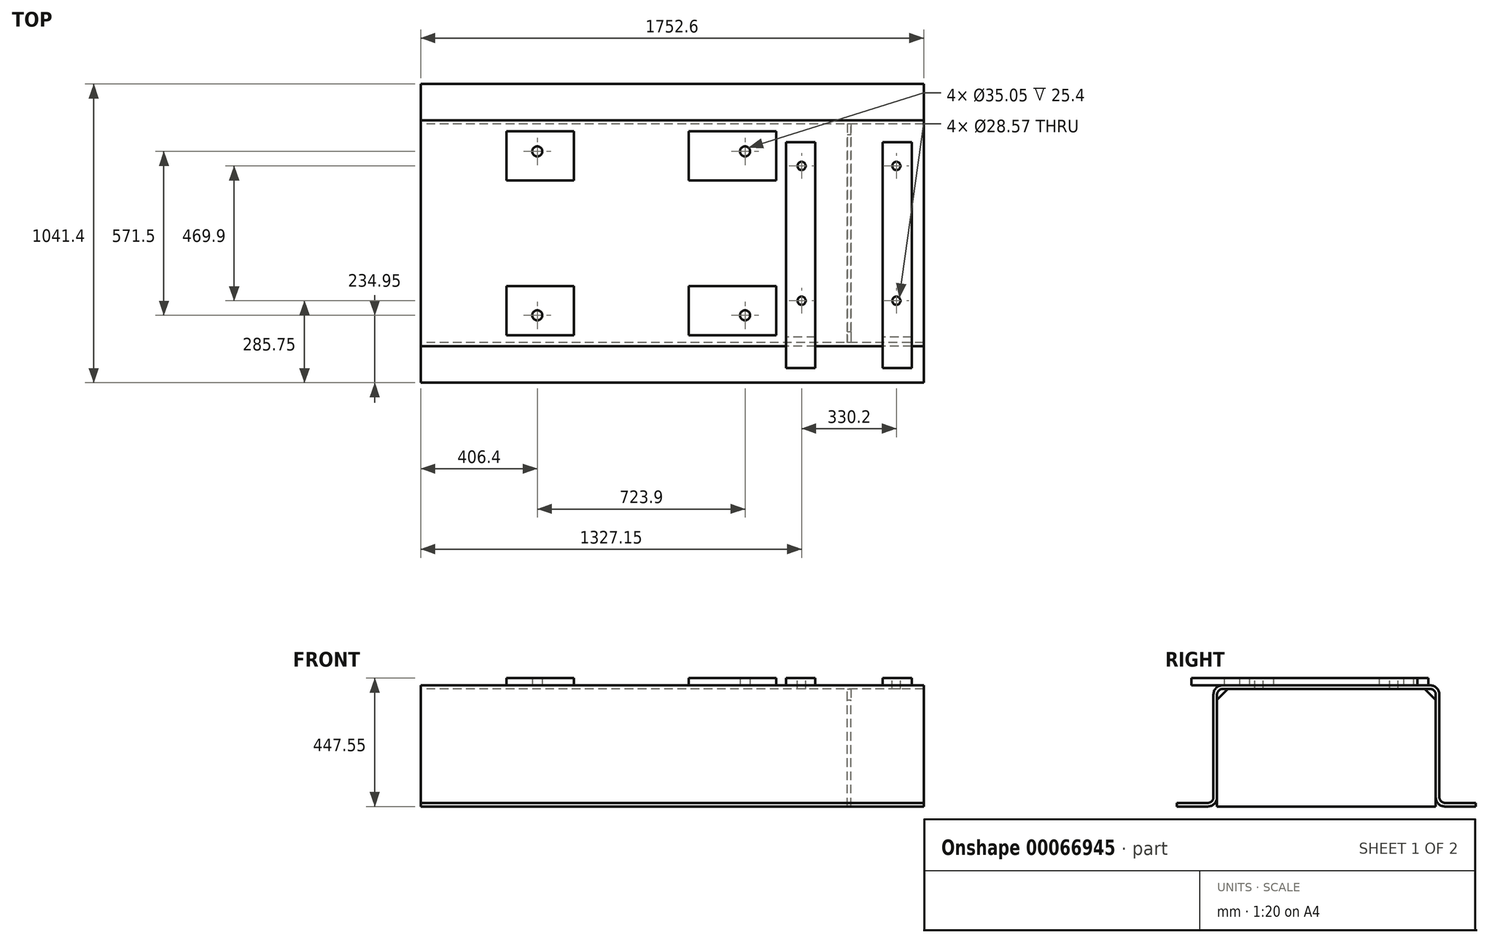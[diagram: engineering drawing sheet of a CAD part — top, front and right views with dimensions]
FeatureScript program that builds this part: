
annotation { "Feature Type Name" : "Feature", "Feature Type Description" : "" }
export const myFeature = defineFeature(function(context is Context, id is Id, definition is map)
    precondition{}
    {
        {
            var Q0;
            Q0=qCreatedBy(makeId("Right.planeOp"),FACE);
            var sketch = newSketch(context, id + "F0", { "sketchPlane" : qUnion([Q0])});
            skLineSegment(sketch, "E0", {"start": v(-520.7, 0) * mm, "end": v(520.7, 0) * mm, "construction": true});
            skLineSegment(sketch, "E1", {"start": v(0, 0) * mm, "end": v(0, 422.15) * mm, "construction": true});
            skLineSegment(sketch, "E2", {"start": v(0, 422.15) * mm, "end": v(361.95, 422.15) * mm});
            skLineSegment(sketch, "E3", {"start": v(393.7, 390.4) * mm, "end": v(393.7, 31.75) * mm});
            skLineSegment(sketch, "E4", {"start": v(412.75, 12.7) * mm, "end": v(520.7, 12.7) * mm});
            skLineSegment(sketch, "E5", {"start": v(520.7, 12.7) * mm, "end": v(520.7, 0) * mm});
            skLineSegment(sketch, "E6", {"start": v(520.7, 0) * mm, "end": v(412.75, 0) * mm});
            skLineSegment(sketch, "E7", {"start": v(381, 31.75) * mm, "end": v(381, 390.4) * mm});
            skLineSegment(sketch, "E8", {"start": v(361.95, 409.45) * mm, "end": v(0, 409.45) * mm});
            skPoint(sketch, "E9.visualSharp", {"position": v(381, 409.45) * mm});
            skArc(sketch, "E9.filletArc", {"start": v(381, 390.4) * mm, "mid": v(375.42, 403.87) * mm, "end": v(361.95, 409.45) * mm});
            skPoint(sketch, "E10.visualSharp", {"position": v(393.7, 12.7) * mm});
            skArc(sketch, "E10.filletArc", {"start": v(393.7, 31.75) * mm, "mid": v(399.28, 18.28) * mm, "end": v(412.75, 12.7) * mm});
            skPoint(sketch, "E11.visualSharp", {"position": v(393.7, 422.15) * mm});
            skArc(sketch, "E11.filletArc", {"start": v(393.7, 390.4) * mm, "mid": v(384.4, 412.85) * mm, "end": v(361.95, 422.15) * mm});
            skPoint(sketch, "E12.visualSharp", {"position": v(381, 0) * mm});
            skArc(sketch, "E12.filletArc", {"start": v(381, 31.75) * mm, "mid": v(390.3, 9.3) * mm, "end": v(412.75, 0) * mm});
            skLineSegment(sketch, "E13.MirrorCS", {"start": v(-520.7, 12.7) * mm, "end": v(-520.7, 0) * mm});
            skArc(sketch, "E14.MirrorCS", {"start": v(-381, 390.4) * mm, "mid": v(-375.42, 403.87) * mm, "end": v(-361.95, 409.45) * mm});
            skArc(sketch, "E15.MirrorCS", {"start": v(-393.7, 31.75) * mm, "mid": v(-399.28, 18.28) * mm, "end": v(-412.75, 12.7) * mm});
            skArc(sketch, "E16.MirrorCS", {"start": v(-381, 31.75) * mm, "mid": v(-390.3, 9.3) * mm, "end": v(-412.75, 0) * mm});
            skArc(sketch, "E17.MirrorCS", {"start": v(-393.7, 390.4) * mm, "mid": v(-384.4, 412.85) * mm, "end": v(-361.95, 422.15) * mm});
            skLineSegment(sketch, "E18.MirrorCS", {"start": v(520.7, 0) * mm, "end": v(-520.7, 0) * mm, "construction": true});
            skPoint(sketch, "E19.MirrorP", {"position": v(-393.7, 422.15) * mm});
            skPoint(sketch, "E20.MirrorP", {"position": v(-381, 409.45) * mm});
            skPoint(sketch, "E21.MirrorP", {"position": v(-393.7, 12.7) * mm});
            skLineSegment(sketch, "E22.MirrorCS", {"start": v(0, 422.15) * mm, "end": v(-361.95, 422.15) * mm});
            skLineSegment(sketch, "E23.MirrorCS", {"start": v(-393.7, 390.4) * mm, "end": v(-393.7, 31.75) * mm});
            skLineSegment(sketch, "E24.MirrorCS", {"start": v(-520.7, 0) * mm, "end": v(-412.75, 0) * mm});
            skLineSegment(sketch, "E25.MirrorCS", {"start": v(-381, 31.75) * mm, "end": v(-381, 390.4) * mm});
            skLineSegment(sketch, "E26.MirrorCS", {"start": v(-361.95, 409.45) * mm, "end": v(0, 409.45) * mm});
            skLineSegment(sketch, "E27.MirrorCS", {"start": v(-412.75, 12.7) * mm, "end": v(-520.7, 12.7) * mm});
            skPoint(sketch, "E28.MirrorP", {"position": v(-381, 0) * mm});
            skSolve(sketch);
        }
        {
            var Q0;
            Q0 = qSketchRegion(id + "F0", true);
            extrude(context, id + "F1", {"entities" : qUnion([Q0]), "endBound" : BoundingType.SYMMETRIC, "depth" : 1752.6 * mm});
        }
        {
            var Q0;
            Q0=makeQuery(id+"F1.opExtrude","SWEPT_FACE",FACE,{"disambiguationData":[OSD([sQuery(id+"F0.wireOp",EDGE,"E2"),sQuery(id+"F0.wireOp",EDGE,"E22.MirrorCS")])]});
            var sketch = newSketch(context, id + "F2", { "sketchPlane" : qUnion([Q0])});
            skLineSegment(sketch, "E29.0", {"start": v(-1765.3, -1196.64) * mm, "end": v(-1765.3, 361.95) * mm, "construction": true});
            skLineSegment(sketch, "E30.0", {"start": v(-1257.3, -1196.64) * mm, "end": v(-1257.3, 361.95) * mm, "construction": true});
            skLineSegment(sketch, "E31.0", {"start": v(-107.95, -1196.64) * mm, "end": v(-107.95, 361.95) * mm, "construction": true});
            skLineSegment(sketch, "E32.0", {"start": v(615.95, -1196.64) * mm, "end": v(615.95, 361.95) * mm, "construction": true});
            skLineSegment(sketch, "E33", {"start": v(-1935.84, 0) * mm, "end": v(1124.96, 0) * mm, "construction": true});
            skLineSegment(sketch, "E34.0", {"start": v(-342.9, -1196.64) * mm, "end": v(-342.9, 361.95) * mm, "construction": true});
            skLineSegment(sketch, "E35.0", {"start": v(-577.85, -1196.64) * mm, "end": v(-577.85, 361.95) * mm, "construction": true});
            skLineSegment(sketch, "E36.0", {"start": v(57.15, -1196.64) * mm, "end": v(57.15, 361.95) * mm, "construction": true});
            skLineSegment(sketch, "E37.0", {"start": v(361.95, -1196.64) * mm, "end": v(361.95, 361.95) * mm, "construction": true});
            skLineSegment(sketch, "E38.0", {"start": v(-1935.84, -184.15) * mm, "end": v(1124.96, -184.15) * mm, "construction": true});
            skLineSegment(sketch, "E39.0", {"start": v(-1935.84, -355.6) * mm, "end": v(1124.96, -355.6) * mm, "construction": true});
            skLineSegment(sketch, "E40.bottom", {"start": v(-342.9, -355.6) * mm, "end": v(-577.85, -355.6) * mm});
            skLineSegment(sketch, "E40.top", {"start": v(-342.9, -184.15) * mm, "end": v(-577.85, -184.15) * mm});
            skLineSegment(sketch, "E40.left", {"start": v(-342.9, -355.6) * mm, "end": v(-342.9, -184.15) * mm});
            skLineSegment(sketch, "E40.right", {"start": v(-577.85, -355.6) * mm, "end": v(-577.85, -184.15) * mm});
            skLineSegment(sketch, "E41.bottom", {"start": v(57.15, -184.15) * mm, "end": v(361.95, -184.15) * mm});
            skLineSegment(sketch, "E41.top", {"start": v(57.15, -355.6) * mm, "end": v(361.95, -355.6) * mm});
            skLineSegment(sketch, "E41.left", {"start": v(57.15, -184.15) * mm, "end": v(57.15, -355.6) * mm});
            skLineSegment(sketch, "E41.right", {"start": v(361.95, -184.15) * mm, "end": v(361.95, -355.6) * mm});
            skLineSegment(sketch, "E42.0", {"start": v(-469.9, -1196.64) * mm, "end": v(-469.9, 361.95) * mm, "construction": true});
            skLineSegment(sketch, "E43.0", {"start": v(254, -1196.64) * mm, "end": v(254, 361.95) * mm, "construction": true});
            skLineSegment(sketch, "E44.0", {"start": v(-1935.84, -285.75) * mm, "end": v(1124.96, -285.75) * mm, "construction": true});
            skCircle(sketch, "E45", {"center": v(-469.9, -285.75) * mm, "radius": 17.53 * mm});
            skCircle(sketch, "E46", {"center": v(254, -285.75) * mm, "radius": 17.53 * mm});
            skCircle(sketch, "E47.MirrorC", {"center": v(-469.9, 285.75) * mm, "radius": 17.53 * mm});
            skLineSegment(sketch, "E48.MirrorCS", {"start": v(-342.9, 355.6) * mm, "end": v(-342.9, 184.15) * mm});
            skCircle(sketch, "E49.MirrorC", {"center": v(254, 285.75) * mm, "radius": 17.53 * mm});
            skLineSegment(sketch, "E50.MirrorCS", {"start": v(57.15, 184.15) * mm, "end": v(361.95, 184.15) * mm});
            skLineSegment(sketch, "E51.MirrorCS", {"start": v(-577.85, 355.6) * mm, "end": v(-577.85, 184.15) * mm});
            skLineSegment(sketch, "E52.MirrorCS", {"start": v(57.15, 355.6) * mm, "end": v(361.95, 355.6) * mm});
            skLineSegment(sketch, "E53.MirrorCS", {"start": v(57.15, 184.15) * mm, "end": v(57.15, 355.6) * mm});
            skLineSegment(sketch, "E54.MirrorCS", {"start": v(-342.9, 184.15) * mm, "end": v(-577.85, 184.15) * mm});
            skLineSegment(sketch, "E55.MirrorCS", {"start": v(361.95, 184.15) * mm, "end": v(361.95, 355.6) * mm});
            skLineSegment(sketch, "E56.MirrorCS", {"start": v(-342.9, 355.6) * mm, "end": v(-577.85, 355.6) * mm});
            skSolve(sketch);
        }
        {
            var Q0;
            Q0 = qSketchRegion(id + "F2", true);
            extrude(context, id + "F3", {"entities" : qUnion([Q0]), "operationType" : NewBodyOperationType.ADD, "depth" : 25.4 * mm});
        }
        {
            var Q0;
            Q0=makeQuery(id+"F2.imprint","IMPRINT",FACE,{"disambiguationData":[TD([[makeQuery(id+"F2.imprint","IMPRINT",EDGE,{"derivedFrom":sQuery(id+"F2.wireOp",EDGE,"E40.bottom")}),1.0]])]});
            var sketch = newSketch(context, id + "F4", { "sketchPlane" : qUnion([Q0])});
            skLineSegment(sketch, "E57.0", {"start": v(615.95, -1196.64) * mm, "end": v(615.95, 361.95) * mm, "construction": true});
            skLineSegment(sketch, "E58.0", {"start": v(498.6, -1196.64) * mm, "end": v(498.6, 361.95) * mm, "construction": true});
            skLineSegment(sketch, "E59.0", {"start": v(397, -1196.64) * mm, "end": v(397, 361.95) * mm, "construction": true});
            skLineSegment(sketch, "E60.0", {"start": v(-1935.84, 317.5) * mm, "end": v(1124.96, 317.5) * mm, "construction": true});
            skLineSegment(sketch, "E61.bottom", {"start": v(397, 317.5) * mm, "end": v(498.6, 317.5) * mm});
            skLineSegment(sketch, "E61.top", {"start": v(397, -469.9) * mm, "end": v(498.6, -469.9) * mm});
            skLineSegment(sketch, "E61.left", {"start": v(397, 317.5) * mm, "end": v(397, -469.9) * mm});
            skLineSegment(sketch, "E61.right", {"start": v(498.6, 317.5) * mm, "end": v(498.6, -469.9) * mm});
            skLineSegment(sketch, "E62.MirrorCS", {"start": v(834.9, -469.9) * mm, "end": v(733.3, -469.9) * mm});
            skLineSegment(sketch, "E63.MirrorCS", {"start": v(834.9, 317.5) * mm, "end": v(733.3, 317.5) * mm});
            skLineSegment(sketch, "E64.MirrorCS", {"start": v(733.3, 317.5) * mm, "end": v(733.3, -469.9) * mm});
            skLineSegment(sketch, "E65.MirrorCS", {"start": v(834.9, 317.5) * mm, "end": v(834.9, -469.9) * mm});
            skSolve(sketch);
        }
        {
            var Q0;
            Q0 = qSketchRegion(id + "F4", true);
            extrude(context, id + "F5", {"entities" : qUnion([Q0]), "operationType" : NewBodyOperationType.ADD, "depth" : 25.4 * mm});
        }
        {
            var Q0;
            Q0=makeQuery(id+"F5.opExtrude","CAP_FACE",FACE,{"disambiguationData":[OSD([sQuery(id+"F4.wireOp",EDGE,"E61.bottom"),sQuery(id+"F4.wireOp",EDGE,"E61.top"),sQuery(id+"F4.wireOp",EDGE,"E61.left"),sQuery(id+"F4.wireOp",EDGE,"E61.right")])],"isStart":false});
            var sketch = newSketch(context, id + "F6", { "sketchPlane" : qUnion([Q0])});
            skLineSegment(sketch, "E66.0", {"start": v(615.95, -1196.64) * mm, "end": v(615.95, 361.95) * mm, "construction": true});
            skLineSegment(sketch, "E67.0", {"start": v(-1935.84, 0) * mm, "end": v(1124.96, 0) * mm, "construction": true});
            skLineSegment(sketch, "E68.0", {"start": v(-1935.84, -234.95) * mm, "end": v(1124.96, -234.95) * mm, "construction": true});
            skLineSegment(sketch, "E69.0", {"start": v(-1935.84, 234.95) * mm, "end": v(1124.96, 234.95) * mm, "construction": true});
            skLineSegment(sketch, "E70.0", {"start": v(450.85, -1196.64) * mm, "end": v(450.85, 361.95) * mm, "construction": true});
            skLineSegment(sketch, "E71.0", {"start": v(781.05, -1196.64) * mm, "end": v(781.05, 361.95) * mm, "construction": true});
            skPoint(sketch, "E72", {"position": v(450.85, 234.95) * mm});
            skPoint(sketch, "E73", {"position": v(781.05, 234.95) * mm});
            skPoint(sketch, "E74", {"position": v(450.85, -234.95) * mm});
            skPoint(sketch, "E75", {"position": v(781.05, -234.95) * mm});
            skSolve(sketch);
        }
        {
            var Q0;
            Q0=sQuery(id+"F6.wireOp",VERTEX,"E72");
            var Q1;
            Q1=sQuery(id+"F6.wireOp",VERTEX,"E73");
            var Q2;
            Q2=sQuery(id+"F6.wireOp",VERTEX,"E74");
            var Q3;
            Q3=sQuery(id+"F6.wireOp",VERTEX,"E75");
            var Q4;
            Q4=makeQuery(id+"F1.opExtrude","SWEPT_BODY",BODY,{"disambiguationData":[OSD([sQuery(id+"F0.wireOp",EDGE,"E2"),sQuery(id+"F0.wireOp",EDGE,"E3"),sQuery(id+"F0.wireOp",EDGE,"E4"),sQuery(id+"F0.wireOp",EDGE,"E5"),sQuery(id+"F0.wireOp",EDGE,"E6"),sQuery(id+"F0.wireOp",EDGE,"E7"),sQuery(id+"F0.wireOp",EDGE,"E8"),sQuery(id+"F0.wireOp",EDGE,"E9.filletArc"),sQuery(id+"F0.wireOp",EDGE,"E10.filletArc"),sQuery(id+"F0.wireOp",EDGE,"E11.filletArc"),sQuery(id+"F0.wireOp",EDGE,"E12.filletArc"),sQuery(id+"F0.wireOp",EDGE,"E13.MirrorCS"),sQuery(id+"F0.wireOp",EDGE,"E14.MirrorCS"),sQuery(id+"F0.wireOp",EDGE,"E15.MirrorCS"),sQuery(id+"F0.wireOp",EDGE,"E16.MirrorCS"),sQuery(id+"F0.wireOp",EDGE,"E17.MirrorCS"),sQuery(id+"F0.wireOp",EDGE,"E22.MirrorCS"),sQuery(id+"F0.wireOp",EDGE,"E23.MirrorCS"),sQuery(id+"F0.wireOp",EDGE,"E24.MirrorCS"),sQuery(id+"F0.wireOp",EDGE,"E25.MirrorCS"),sQuery(id+"F0.wireOp",EDGE,"E26.MirrorCS"),sQuery(id+"F0.wireOp",EDGE,"E27.MirrorCS")])]});
            hole(context, id + "F7", {"style" : HoleStyle.SIMPLE, "holeDiameter" : 28.57 * mm, "endStyle" : HoleEndStyle.THROUGH, "locations" : qUnion([Q0, Q1, Q2, Q3]), "scope" : qUnion([Q4])});
        }
        {
            var Q0;
            Q0=makeQuery(id+"F1.opExtrude","SWEPT_FACE",FACE,{"disambiguationData":[OSD([sQuery(id+"F0.wireOp",EDGE,"E8"),sQuery(id+"F0.wireOp",EDGE,"E26.MirrorCS")])]});
            var sketch = newSketch(context, id + "F8", { "sketchPlane" : qUnion([Q0])});
            skLineSegment(sketch, "E76.0", {"start": v(615.95, 381) * mm, "end": v(615.95, -381) * mm, "construction": true});
            skLineSegment(sketch, "E77.0.1", {"start": v(-876.3, -381) * mm, "end": v(876.3, -381) * mm, "construction": true});
            skLineSegment(sketch, "E77.0.3", {"start": v(876.3, -381) * mm, "end": v(-876.3, -381) * mm, "construction": true});
            skLineSegment(sketch, "E78.0.1", {"start": v(-876.3, 381) * mm, "end": v(876.3, 381) * mm, "construction": true});
            skLineSegment(sketch, "E78.0.3", {"start": v(876.3, 381) * mm, "end": v(-876.3, 381) * mm, "construction": true});
            skPoint(sketch, "E79.orphan", {"position": v(615.95, -361.95) * mm});
            skPoint(sketch, "E80.orphan", {"position": v(615.95, 1196.64) * mm});
            skLineSegment(sketch, "E81.0", {"start": v(609.6, 381) * mm, "end": v(609.6, -381) * mm});
            skLineSegment(sketch, "E82.bottom", {"start": v(609.6, 381) * mm, "end": v(622.3, 381) * mm});
            skLineSegment(sketch, "E82.top", {"start": v(609.6, -381) * mm, "end": v(622.3, -381) * mm});
            skLineSegment(sketch, "E82.right", {"start": v(622.3, 381) * mm, "end": v(622.3, -381) * mm});
            skSolve(sketch);
        }
        {
            var Q0;
            Q0 = qSketchRegion(id + "F8", true);
            var Q1;
            Q1=makeQuery(id+"F1.opExtrude","SWEPT_FACE",FACE,{"disambiguationData":[OSD([sQuery(id+"F0.wireOp",EDGE,"E24.MirrorCS")])]});
            extrude(context, id + "F9", {"entities" : qUnion([Q0]), "endBound" : BoundingType.UP_TO_SURFACE, "endBoundEntityFace" : qUnion([Q1]), "depth" : 25.4 * mm});
        }
        {
            var Q0;
            Q0=makeQuery(id+"F9.opExtrude","CAP_EDGE",EDGE,{"disambiguationData":[OSD([sQuery(id+"F8.wireOp",EDGE,"E82.top")])],"isStart":true});
            var Q1;
            Q1=makeQuery(id+"F9.opExtrude","CAP_EDGE",EDGE,{"disambiguationData":[OSD([sQuery(id+"F8.wireOp",EDGE,"E82.bottom")])],"isStart":true});
            chamfer(context, id + "F10", {"entities" : qUnion([Q0, Q1]), "width" : 38.1 * mm, "tangentPropagation" : true});
        }
    });
